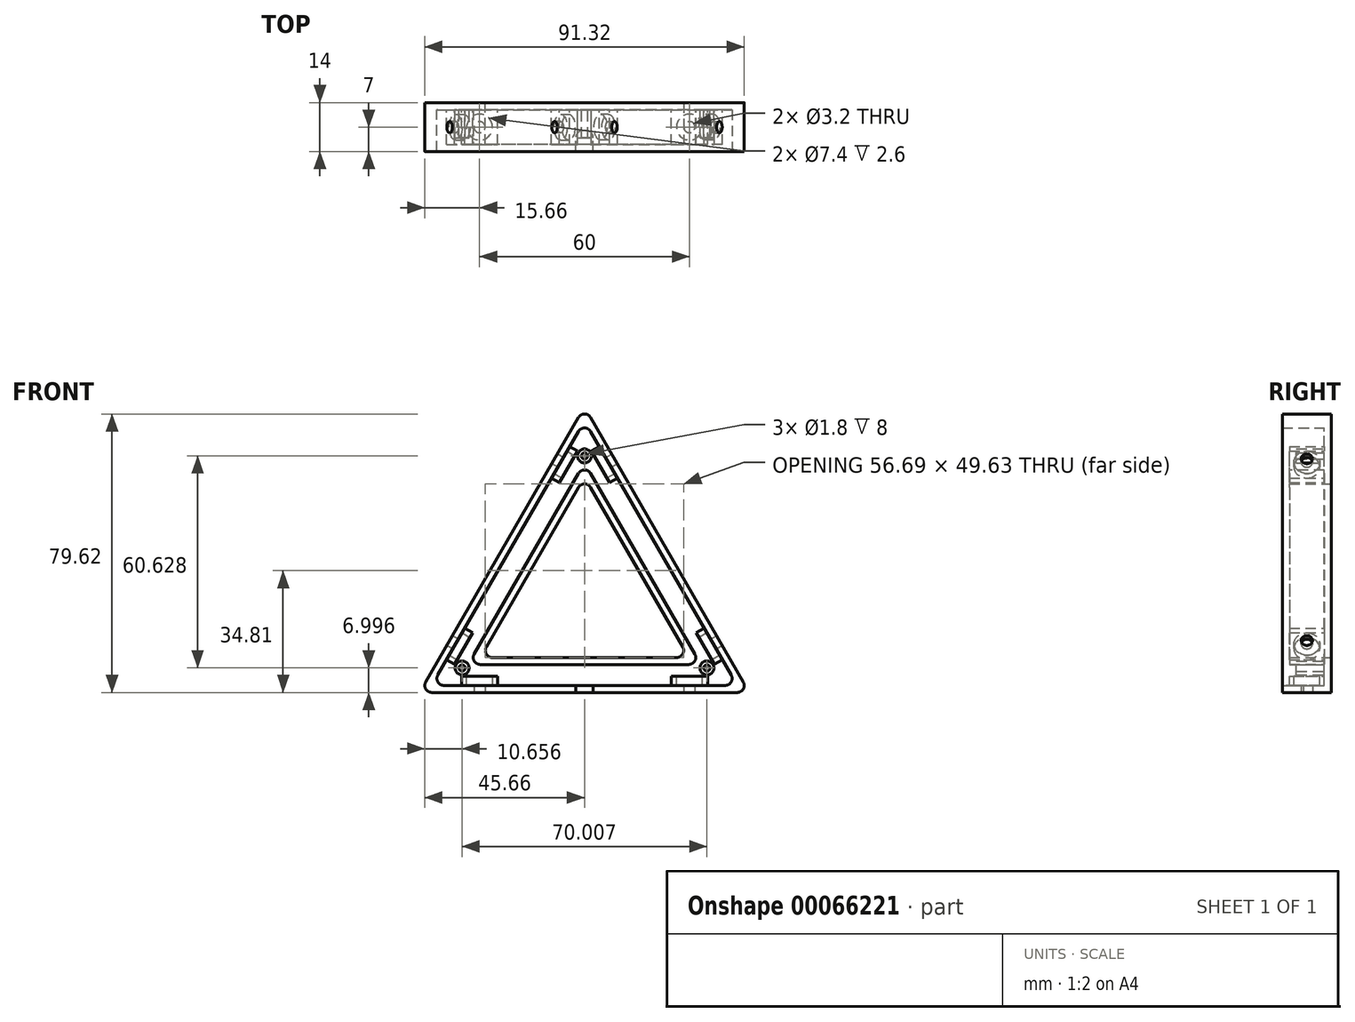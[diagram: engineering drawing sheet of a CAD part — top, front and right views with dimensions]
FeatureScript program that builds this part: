
annotation { "Feature Type Name" : "Feature", "Feature Type Description" : "" }
export const myFeature = defineFeature(function(context is Context, id is Id, definition is map)
    precondition{}
    {
        {
            var Q0;
            Q0=qCreatedBy(makeId("Front.planeOp"),FACE);
            var sketch = newSketch(context, id + "F0", { "sketchPlane" : qUnion([Q0])});
            skLineSegment(sketch, "E0", {"start": v(0, 40.81) * mm, "end": v(-47.13, -40.81) * mm, "construction": true});
            skLineSegment(sketch, "E1", {"start": v(0, 40.81) * mm, "end": v(47.13, -40.81) * mm, "construction": true});
            skLineSegment(sketch, "E2", {"start": v(47.13, -40.81) * mm, "end": v(-47.13, -40.81) * mm, "construction": true});
            skLineSegment(sketch, "E3", {"start": v(0, 40.81) * mm, "end": v(-47.13, -40.81) * mm});
            skLineSegment(sketch, "E4", {"start": v(47.13, -40.81) * mm, "end": v(-47.13, -40.81) * mm});
            skLineSegment(sketch, "E5", {"start": v(0, 40.81) * mm, "end": v(47.13, -40.81) * mm});
            skLineSegment(sketch, "E6", {"start": v(0, 40.81) * mm, "end": v(0, -40.81) * mm, "construction": true});
            skLineSegment(sketch, "E7", {"start": v(0, -40.81) * mm, "end": v(0, 0) * mm, "construction": true});
            skLineSegment(sketch, "E8.0", {"start": v(0, 20.81) * mm, "end": v(29.8, -30.81) * mm});
            skLineSegment(sketch, "E8.1", {"start": v(0, 20.81) * mm, "end": v(-29.8, -30.81) * mm});
            skLineSegment(sketch, "E8.2", {"start": v(29.8, -30.81) * mm, "end": v(-29.8, -30.81) * mm});
            skSolve(sketch);
        }
        {
            var Q0;
            Q0=qSketchRegion(id+"F0",true);
            extrude(context, id + "F1", {"entities" : qUnion([Q0]), "depth" : 2 * mm});
        }
        {
            var Q0;
            Q0=makeQuery(id+"F1.opExtrude","CAP_FACE",FACE,{"disambiguationData":[OSD([sQuery(id+"F0.wireOp",EDGE,"E3"),sQuery(id+"F0.wireOp",EDGE,"E4"),sQuery(id+"F0.wireOp",EDGE,"E5"),sQuery(id+"F0.wireOp",EDGE,"1c6YzCQz-RSOc-zTex-pMTN-9Ec4khBtqjMo"),sQuery(id+"F0.wireOp",EDGE,"E1i0Fd6E-5Ke1-2Vyi-b1Zw-UHEibEwRgWVJ"),sQuery(id+"F0.wireOp",EDGE,"lRk4sWtj-3Wfv-Gcz0-gw5n-paqTTmhbEHYp")])],"isStart":false});
            var sketch = newSketch(context, id + "F2", { "sketchPlane" : qUnion([Q0])});
            skLineSegment(sketch, "E9", {"start": v(-47.13, -40.81) * mm, "end": v(0, 40.81) * mm});
            skLineSegment(sketch, "E10.0", {"start": v(-43.66, -38.81) * mm, "end": v(0, 36.81) * mm});
            skLineSegment(sketch, "E11", {"start": v(-47.13, -40.81) * mm, "end": v(47.13, -40.81) * mm});
            skLineSegment(sketch, "E12.0", {"start": v(-43.66, -38.81) * mm, "end": v(43.66, -38.81) * mm});
            skLineSegment(sketch, "E13.MirrorCS", {"start": v(47.13, -40.81) * mm, "end": v(0, 40.81) * mm});
            skLineSegment(sketch, "E14.MirrorCS", {"start": v(43.66, -38.81) * mm, "end": v(0, 36.81) * mm});
            skSolve(sketch);
        }
        {
            var Q0;
            Q0=qSketchRegion(id+"F2",true);
            extrude(context, id + "F3", {"entities" : qUnion([Q0]), "operationType" : NewBodyOperationType.ADD, "depth" : 12 * mm});
        }
        {
            var Q0;
            Q0=makeQuery(id+"F1.opExtrude","CAP_FACE",FACE,{"disambiguationData":[OSD([sQuery(id+"F0.wireOp",EDGE,"E3"),sQuery(id+"F0.wireOp",EDGE,"E4"),sQuery(id+"F0.wireOp",EDGE,"E5"),sQuery(id+"F0.wireOp",EDGE,"1c6YzCQz-RSOc-zTex-pMTN-9Ec4khBtqjMo"),sQuery(id+"F0.wireOp",EDGE,"E1i0Fd6E-5Ke1-2Vyi-b1Zw-UHEibEwRgWVJ"),sQuery(id+"F0.wireOp",EDGE,"lRk4sWtj-3Wfv-Gcz0-gw5n-paqTTmhbEHYp")])],"isStart":false});
            var sketch = newSketch(context, id + "F4", { "sketchPlane" : qUnion([Q0])});
            skLineSegment(sketch, "E15.0", {"start": v(0, 20.81) * mm, "end": v(29.8, -30.81) * mm});
            skLineSegment(sketch, "E15.1", {"start": v(0, 20.81) * mm, "end": v(-29.8, -30.81) * mm});
            skLineSegment(sketch, "E15.2", {"start": v(29.8, -30.81) * mm, "end": v(-29.8, -30.81) * mm});
            skLineSegment(sketch, "E16.0", {"start": v(0, 24.81) * mm, "end": v(33.27, -32.81) * mm});
            skLineSegment(sketch, "E16.1", {"start": v(0, 24.81) * mm, "end": v(-33.27, -32.81) * mm});
            skLineSegment(sketch, "E16.2", {"start": v(33.27, -32.81) * mm, "end": v(-33.27, -32.81) * mm});
            skSolve(sketch);
        }
        {
            var Q0;
            Q0=qSketchRegion(id+"F4",true);
            extrude(context, id + "F5", {"entities" : qUnion([Q0]), "operationType" : NewBodyOperationType.ADD, "depth" : 10 * mm});
        }
        {
            var Q0;
            Q0=makeQuery(id+"F3.boolean.opBoolean","MERGE",EDGE,{"derivedFrom":[makeQuery(id+"F1.opExtrude","SWEPT_EDGE",EDGE,{"disambiguationData":[OSD([sQuery(id+"F0.wireOp",EDGE,"E4"),sQuery(id+"F0.wireOp",EDGE,"E5")])]}),makeQuery(id+"F3.opExtrude","SWEPT_EDGE",EDGE,{"disambiguationData":[OSD([sQuery(id+"F2.wireOp",EDGE,"E11"),sQuery(id+"F2.wireOp",EDGE,"E13.MirrorCS")])]})]});
            var Q1;
            Q1=makeQuery(id+"F3.boolean.opBoolean","MERGE",EDGE,{"derivedFrom":[makeQuery(id+"F1.opExtrude","SWEPT_EDGE",EDGE,{"disambiguationData":[OSD([sQuery(id+"F0.wireOp",EDGE,"E3"),sQuery(id+"F0.wireOp",EDGE,"E4")])]}),makeQuery(id+"F3.opExtrude","SWEPT_EDGE",EDGE,{"disambiguationData":[OSD([sQuery(id+"F2.wireOp",EDGE,"E9"),sQuery(id+"F2.wireOp",EDGE,"E11")])]})]});
            var Q2;
            Q2=makeQuery(id+"F3.boolean.opBoolean","MERGE",EDGE,{"derivedFrom":[makeQuery(id+"F1.opExtrude","SWEPT_EDGE",EDGE,{"disambiguationData":[OSD([sQuery(id+"F0.wireOp",EDGE,"E3"),sQuery(id+"F0.wireOp",EDGE,"E5")])]}),makeQuery(id+"F3.opExtrude","SWEPT_EDGE",EDGE,{"disambiguationData":[OSD([sQuery(id+"F2.wireOp",EDGE,"E9"),sQuery(id+"F2.wireOp",EDGE,"E13.MirrorCS")])]})]});
            var Q3;
            Q3=makeQuery(id+"F5.opExtrude","SWEPT_EDGE",EDGE,{"disambiguationData":[OSD([sQuery(id+"F4.wireOp",EDGE,"777d23ab-cff7-4353-932e-786e568167e6.0"),sQuery(id+"F4.wireOp",EDGE,"777d23ab-cff7-4353-932e-786e568167e6.1")])]});
            var Q4;
            Q4=makeQuery(id+"F5.opExtrude","SWEPT_EDGE",EDGE,{"disambiguationData":[OSD([sQuery(id+"F4.wireOp",EDGE,"777d23ab-cff7-4353-932e-786e568167e6.1"),sQuery(id+"F4.wireOp",EDGE,"777d23ab-cff7-4353-932e-786e568167e6.2")])]});
            var Q5;
            Q5=makeQuery(id+"F5.opExtrude","SWEPT_EDGE",EDGE,{"disambiguationData":[OSD([sQuery(id+"F4.wireOp",EDGE,"777d23ab-cff7-4353-932e-786e568167e6.0"),sQuery(id+"F4.wireOp",EDGE,"777d23ab-cff7-4353-932e-786e568167e6.2")])]});
            var Q6;
            Q6=makeQuery(id+"F5.boolean.opBoolean","MERGE",EDGE,{"derivedFrom":[makeQuery(id+"F1.opExtrude","SWEPT_EDGE",EDGE,{"disambiguationData":[OSD([sQuery(id+"F0.wireOp",EDGE,"E8.1"),sQuery(id+"F0.wireOp",EDGE,"E8.2")])]}),makeQuery(id+"F5.opExtrude","SWEPT_EDGE",EDGE,{"disambiguationData":[OSD([sQuery(id+"F4.wireOp",EDGE,"E15.1"),sQuery(id+"F4.wireOp",EDGE,"E15.2")])]})]});
            var Q7;
            Q7=makeQuery(id+"F3.opExtrude","SWEPT_EDGE",EDGE,{"disambiguationData":[OSD([sQuery(id+"F2.wireOp",EDGE,"E10.0"),sQuery(id+"F2.wireOp",EDGE,"E12.0")])]});
            var Q8;
            Q8=makeQuery(id+"F5.opExtrude","SWEPT_EDGE",EDGE,{"disambiguationData":[OSD([sQuery(id+"F4.wireOp",EDGE,"E16.0"),sQuery(id+"F4.wireOp",EDGE,"E16.1")])]});
            var Q9;
            Q9=makeQuery(id+"F5.boolean.opBoolean","MERGE",EDGE,{"derivedFrom":[makeQuery(id+"F1.opExtrude","SWEPT_EDGE",EDGE,{"disambiguationData":[OSD([sQuery(id+"F0.wireOp",EDGE,"E8.0"),sQuery(id+"F0.wireOp",EDGE,"E8.1")])]}),makeQuery(id+"F5.opExtrude","SWEPT_EDGE",EDGE,{"disambiguationData":[OSD([sQuery(id+"F4.wireOp",EDGE,"E15.0"),sQuery(id+"F4.wireOp",EDGE,"E15.1")])]})]});
            var Q10;
            Q10=makeQuery(id+"F3.opExtrude","SWEPT_EDGE",EDGE,{"disambiguationData":[OSD([sQuery(id+"F2.wireOp",EDGE,"E10.0"),sQuery(id+"F2.wireOp",EDGE,"E14.MirrorCS")])]});
            var Q11;
            Q11=makeQuery(id+"F5.opExtrude","SWEPT_EDGE",EDGE,{"disambiguationData":[OSD([sQuery(id+"F4.wireOp",EDGE,"E16.0"),sQuery(id+"F4.wireOp",EDGE,"E16.2")])]});
            var Q12;
            Q12=makeQuery(id+"F5.opExtrude","SWEPT_EDGE",EDGE,{"disambiguationData":[OSD([sQuery(id+"F4.wireOp",EDGE,"E16.1"),sQuery(id+"F4.wireOp",EDGE,"E16.2")])]});
            var Q13;
            Q13=makeQuery(id+"F5.boolean.opBoolean","MERGE",EDGE,{"derivedFrom":[makeQuery(id+"F1.opExtrude","SWEPT_EDGE",EDGE,{"disambiguationData":[OSD([sQuery(id+"F0.wireOp",EDGE,"E8.0"),sQuery(id+"F0.wireOp",EDGE,"E8.2")])]}),makeQuery(id+"F5.opExtrude","SWEPT_EDGE",EDGE,{"disambiguationData":[OSD([sQuery(id+"F4.wireOp",EDGE,"E15.0"),sQuery(id+"F4.wireOp",EDGE,"E15.2")])]})]});
            var Q14;
            Q14=makeQuery(id+"F3.opExtrude","SWEPT_EDGE",EDGE,{"disambiguationData":[OSD([sQuery(id+"F2.wireOp",EDGE,"E12.0"),sQuery(id+"F2.wireOp",EDGE,"E14.MirrorCS")])]});
            fillet(context, id + "F6", {"entities" : qUnion([Q0, Q1, Q2, Q3, Q4, Q5, Q6, Q7, Q8, Q9, Q10, Q11, Q12, Q13, Q14]), "radius" : 2 * mm, "tangentPropagation" : true, "allowEdgeOverflow" : false});
        }
        {
            var Q0;
            Q0=makeQuery(id+"F1.opExtrude","CAP_FACE",FACE,{"disambiguationData":[OSD([sQuery(id+"F0.wireOp",EDGE,"E3"),sQuery(id+"F0.wireOp",EDGE,"E4"),sQuery(id+"F0.wireOp",EDGE,"E5"),sQuery(id+"F0.wireOp",EDGE,"E8.0"),sQuery(id+"F0.wireOp",EDGE,"E8.1"),sQuery(id+"F0.wireOp",EDGE,"E8.2")])],"isStart":false});
            var sketch = newSketch(context, id + "F7", { "sketchPlane" : qUnion([Q0])});
            skLineSegment(sketch, "E17", {"start": v(-1.73, 33.81) * mm, "end": v(-4.23, 29.48) * mm, "construction": true});
            skLineSegment(sketch, "E18", {"start": v(-4.23, 29.48) * mm, "end": v(-9.43, 20.48) * mm, "construction": true});
            skLineSegment(sketch, "E19", {"start": v(-9.43, 20.48) * mm, "end": v(-34.23, -22.48) * mm, "construction": true});
            skLineSegment(sketch, "E20", {"start": v(-34.23, -22.48) * mm, "end": v(-39.43, -31.48) * mm, "construction": true});
            skLineSegment(sketch, "E21", {"start": v(-39.43, -31.48) * mm, "end": v(-41.93, -35.81) * mm, "construction": true});
            skLineSegment(sketch, "E22", {"start": v(-41.93, -37.81) * mm, "end": v(21.83, -1) * mm, "construction": true});
            skLineSegment(sketch, "E23", {"start": v(-4.23, 29.48) * mm, "end": v(-1.98, 28.18) * mm, "construction": true});
            skLineSegment(sketch, "E24", {"start": v(-34.23, -22.48) * mm, "end": v(-31.98, -23.78) * mm});
            skLineSegment(sketch, "E25", {"start": v(-9.43, 20.48) * mm, "end": v(-7.18, 19.18) * mm, "construction": true});
            skLineSegment(sketch, "E26", {"start": v(-39.43, -31.48) * mm, "end": v(-37.18, -32.78) * mm});
            skLineSegment(sketch, "E27", {"start": v(-7.18, 19.18) * mm, "end": v(-1.98, 28.18) * mm});
            skLineSegment(sketch, "E28", {"start": v(-4.23, 29.48) * mm, "end": v(-1.98, 28.18) * mm});
            skLineSegment(sketch, "E29", {"start": v(-7.18, 19.18) * mm, "end": v(-9.43, 20.48) * mm});
            skLineSegment(sketch, "E30", {"start": v(-9.43, 20.48) * mm, "end": v(-4.23, 29.48) * mm});
            skLineSegment(sketch, "E31", {"start": v(-31.98, -23.78) * mm, "end": v(-37.18, -32.78) * mm});
            skLineSegment(sketch, "E32", {"start": v(-39.43, -31.48) * mm, "end": v(-34.23, -22.48) * mm});
            skLineSegment(sketch, "E33.MirrorCS", {"start": v(4.23, 29.48) * mm, "end": v(1.98, 28.18) * mm, "construction": true});
            skLineSegment(sketch, "E34.MirrorCS", {"start": v(9.43, 20.48) * mm, "end": v(7.18, 19.18) * mm, "construction": true});
            skLineSegment(sketch, "E35.MirrorCS", {"start": v(4.23, 29.48) * mm, "end": v(1.98, 28.18) * mm});
            skLineSegment(sketch, "E36.MirrorCS", {"start": v(7.18, 19.18) * mm, "end": v(9.43, 20.48) * mm});
            skLineSegment(sketch, "E37.MirrorCS", {"start": v(34.23, -22.48) * mm, "end": v(31.98, -23.78) * mm});
            skLineSegment(sketch, "E38.MirrorCS", {"start": v(39.43, -31.48) * mm, "end": v(37.18, -32.78) * mm});
            skLineSegment(sketch, "E39.MirrorCS", {"start": v(4.23, 29.48) * mm, "end": v(9.43, 20.48) * mm, "construction": true});
            skLineSegment(sketch, "E40.MirrorCS", {"start": v(34.23, -22.48) * mm, "end": v(39.43, -31.48) * mm, "construction": true});
            skLineSegment(sketch, "E41.MirrorCS", {"start": v(9.43, 20.48) * mm, "end": v(34.23, -22.48) * mm, "construction": true});
            skLineSegment(sketch, "E42.MirrorCS", {"start": v(39.43, -31.48) * mm, "end": v(41.93, -35.81) * mm, "construction": true});
            skLineSegment(sketch, "E43.MirrorCS", {"start": v(1.73, 33.81) * mm, "end": v(4.23, 29.48) * mm, "construction": true});
            skLineSegment(sketch, "E44.MirrorCS", {"start": v(39.43, -31.48) * mm, "end": v(34.23, -22.48) * mm});
            skLineSegment(sketch, "E45.MirrorCS", {"start": v(31.98, -23.78) * mm, "end": v(37.18, -32.78) * mm});
            skLineSegment(sketch, "E46.MirrorCS", {"start": v(9.43, 20.48) * mm, "end": v(4.23, 29.48) * mm});
            skLineSegment(sketch, "E47.MirrorCS", {"start": v(7.18, 19.18) * mm, "end": v(1.98, 28.18) * mm});
            skLineSegment(sketch, "E48.MirrorCS", {"start": v(35.2, -38.81) * mm, "end": v(35.2, -36.21) * mm, "construction": true});
            skLineSegment(sketch, "E49.MirrorCS", {"start": v(24.8, -38.81) * mm, "end": v(24.8, -36.21) * mm, "construction": true});
            skLineSegment(sketch, "E50.MirrorCS", {"start": v(35.2, -38.81) * mm, "end": v(35.2, -36.21) * mm});
            skLineSegment(sketch, "E51.MirrorCS", {"start": v(24.8, -36.21) * mm, "end": v(24.8, -38.81) * mm});
            skLineSegment(sketch, "E52.MirrorCS", {"start": v(-24.8, -38.81) * mm, "end": v(-24.8, -36.21) * mm});
            skLineSegment(sketch, "E53.MirrorCS", {"start": v(-35.2, -38.81) * mm, "end": v(-35.2, -36.21) * mm});
            skLineSegment(sketch, "E54.MirrorCS", {"start": v(35.2, -38.81) * mm, "end": v(24.8, -38.81) * mm, "construction": true});
            skLineSegment(sketch, "E55.MirrorCS", {"start": v(-24.8, -38.81) * mm, "end": v(-35.2, -38.81) * mm, "construction": true});
            skLineSegment(sketch, "E56.MirrorCS", {"start": v(40.2, -38.81) * mm, "end": v(35.2, -38.81) * mm, "construction": true});
            skLineSegment(sketch, "E57.MirrorCS", {"start": v(-35.2, -38.81) * mm, "end": v(-24.8, -38.81) * mm});
            skLineSegment(sketch, "E58.MirrorCS", {"start": v(-24.8, -36.21) * mm, "end": v(-35.2, -36.21) * mm});
            skLineSegment(sketch, "E59.MirrorCS", {"start": v(24.8, -38.81) * mm, "end": v(35.2, -38.81) * mm});
            skLineSegment(sketch, "E60.MirrorCS", {"start": v(-35.2, -38.81) * mm, "end": v(-40.2, -38.81) * mm, "construction": true});
            skLineSegment(sketch, "E61.MirrorCS", {"start": v(24.8, -38.81) * mm, "end": v(-24.8, -38.81) * mm, "construction": true});
            skLineSegment(sketch, "E62.MirrorCS", {"start": v(24.8, -36.21) * mm, "end": v(35.2, -36.21) * mm});
            skPoint(sketch, "E63", {"position": v(-36.83, -26.98) * mm});
            skPoint(sketch, "E64", {"position": v(-6.83, 24.98) * mm});
            skSolve(sketch);
        }
        {
            var Q0;
            Q0=qSketchRegion(id+"F7",true);
            extrude(context, id + "F8", {"entities" : qUnion([Q0]), "operationType" : NewBodyOperationType.ADD, "depth" : 10 * mm});
        }
        {
            var Q0;
            Q0=makeQuery(id+"F3.boolean.opBoolean","MERGE",FACE,{"derivedFrom":[makeQuery(id+"F1.opExtrude","SWEPT_FACE",FACE,{"disambiguationData":[OSD([sQuery(id+"F0.wireOp",EDGE,"E4")])]}),makeQuery(id+"F3.opExtrude","SWEPT_FACE",FACE,{"disambiguationData":[OSD([sQuery(id+"F2.wireOp",EDGE,"E11")])]})]});
            var sketch = newSketch(context, id + "F9", { "sketchPlane" : qUnion([Q0])});
            skLineSegment(sketch, "E65", {"start": v(-43.66, 14) * mm, "end": v(43.66, 14) * mm, "construction": true});
            skLineSegment(sketch, "E66", {"start": v(43.66, 14) * mm, "end": v(0, 14) * mm, "construction": true});
            skLineSegment(sketch, "E67", {"start": v(0, 14) * mm, "end": v(2.5, 14) * mm, "construction": true});
            skLineSegment(sketch, "E68", {"start": v(0, 14) * mm, "end": v(-2.5, 14) * mm, "construction": true});
            skLineSegment(sketch, "E69", {"start": v(-2.5, 14) * mm, "end": v(-2.5, 8) * mm, "construction": true});
            skLineSegment(sketch, "E70.bottom", {"start": v(2.5, 14) * mm, "end": v(-2.5, 14) * mm});
            skLineSegment(sketch, "E70.top", {"start": v(2.5, 8) * mm, "end": v(-2.5, 8) * mm});
            skLineSegment(sketch, "E70.left", {"start": v(2.5, 14) * mm, "end": v(2.5, 8) * mm});
            skLineSegment(sketch, "E70.right", {"start": v(-2.5, 14) * mm, "end": v(-2.5, 8) * mm});
            skLineSegment(sketch, "E71.0", {"start": v(-24.8, 12) * mm, "end": v(-24.8, 2) * mm, "construction": true});
            skLineSegment(sketch, "E71.1", {"start": v(-35.2, 12) * mm, "end": v(-35.2, 2) * mm, "construction": true});
            skLineSegment(sketch, "E71.2", {"start": v(24.8, 12) * mm, "end": v(24.8, 2) * mm, "construction": true});
            skLineSegment(sketch, "E71.3", {"start": v(35.2, 12) * mm, "end": v(35.2, 2) * mm, "construction": true});
            skLineSegment(sketch, "E72", {"start": v(-35.2, 7) * mm, "end": v(-24.8, 7) * mm, "construction": true});
            skLineSegment(sketch, "E73", {"start": v(-24.8, 7) * mm, "end": v(-30, 7) * mm, "construction": true});
            skLineSegment(sketch, "E74", {"start": v(-30, 7) * mm, "end": v(24.8, 7) * mm, "construction": true});
            skLineSegment(sketch, "E75", {"start": v(24.8, 7) * mm, "end": v(35.2, 7) * mm, "construction": true});
            skLineSegment(sketch, "E76", {"start": v(35.2, 7) * mm, "end": v(30, 7) * mm, "construction": true});
            skCircle(sketch, "E77", {"center": v(-30, 7) * mm, "radius": 1.6 * mm});
            skCircle(sketch, "E78", {"center": v(30, 7) * mm, "radius": 1.6 * mm});
            skSolve(sketch);
        }
        {
            var Q0;
            Q0=qSketchRegion(id+"F9",true);
            extrude(context, id + "F10", {"entities" : qUnion([Q0]), "operationType" : NewBodyOperationType.REMOVE, "oppositeDirection" : true, "depth" : 5 * mm});
        }
        {
            var Q0;
            Q0=makeQuery(id+"F3.boolean.opBoolean","MERGE",FACE,{"derivedFrom":[makeQuery(id+"F1.opExtrude","SWEPT_FACE",FACE,{"disambiguationData":[OSD([sQuery(id+"F0.wireOp",EDGE,"E5")])]}),makeQuery(id+"F3.opExtrude","SWEPT_FACE",FACE,{"disambiguationData":[OSD([sQuery(id+"F2.wireOp",EDGE,"E13.MirrorCS")])]})]});
            var sketch = newSketch(context, id + "F11", { "sketchPlane" : qUnion([Q0])});
            skLineSegment(sketch, "E79", {"start": v(-14, 31.88) * mm, "end": v(-14, -55.45) * mm, "construction": true});
            skLineSegment(sketch, "E80", {"start": v(-14, -55.45) * mm, "end": v(-14, -11.78) * mm, "construction": true});
            skLineSegment(sketch, "E81", {"start": v(-14, -11.78) * mm, "end": v(-14, -9.28) * mm, "construction": true});
            skLineSegment(sketch, "E82", {"start": v(-14, -9.28) * mm, "end": v(-14, -14.28) * mm, "construction": true});
            skLineSegment(sketch, "E83", {"start": v(-14, -14.28) * mm, "end": v(-8, -14.28) * mm, "construction": true});
            skLineSegment(sketch, "E84.bottom", {"start": v(-14, -9.28) * mm, "end": v(-8, -9.28) * mm, "construction": true});
            skLineSegment(sketch, "E84.right", {"start": v(-8, -9.28) * mm, "end": v(-8, -14.28) * mm, "construction": true});
            skLineSegment(sketch, "E85.0", {"start": v(-12, 13.02) * mm, "end": v(-2, 13.02) * mm, "construction": true});
            skLineSegment(sketch, "E85.1", {"start": v(-12, 23.42) * mm, "end": v(-2, 23.42) * mm, "construction": true});
            skLineSegment(sketch, "E85.2", {"start": v(-12, -46.98) * mm, "end": v(-2, -46.98) * mm, "construction": true});
            skLineSegment(sketch, "E85.3", {"start": v(-12, -36.58) * mm, "end": v(-2, -36.58) * mm, "construction": true});
            skLineSegment(sketch, "E86", {"start": v(-7, -46.98) * mm, "end": v(-7, -36.58) * mm, "construction": true});
            skLineSegment(sketch, "E87", {"start": v(-7, -36.58) * mm, "end": v(-7, -41.78) * mm, "construction": true});
            skLineSegment(sketch, "E88", {"start": v(-7, -41.78) * mm, "end": v(-7, 13.02) * mm, "construction": true});
            skLineSegment(sketch, "E89", {"start": v(-7, 13.02) * mm, "end": v(-7, 23.42) * mm, "construction": true});
            skLineSegment(sketch, "E90", {"start": v(-7, 23.42) * mm, "end": v(-7, 18.22) * mm, "construction": true});
            skCircle(sketch, "E91", {"center": v(-7, 18.22) * mm, "radius": 1.6 * mm});
            skCircle(sketch, "E92", {"center": v(-7, -41.78) * mm, "radius": 1.6 * mm});
            skSolve(sketch);
        }
        {
            var Q0;
            Q0=qSketchRegion(id+"F11",true);
            extrude(context, id + "F12", {"entities" : qUnion([Q0]), "operationType" : NewBodyOperationType.REMOVE, "oppositeDirection" : true, "depth" : 5 * mm});
        }
        {
            var Q0;
            Q0=makeQuery(id+"F3.boolean.opBoolean","MERGE",FACE,{"derivedFrom":[makeQuery(id+"F1.opExtrude","SWEPT_FACE",FACE,{"disambiguationData":[OSD([sQuery(id+"F0.wireOp",EDGE,"E3")])]}),makeQuery(id+"F3.opExtrude","SWEPT_FACE",FACE,{"disambiguationData":[OSD([sQuery(id+"F2.wireOp",EDGE,"E9")])]})]});
            var sketch = newSketch(context, id + "F13", { "sketchPlane" : qUnion([Q0])});
            skLineSegment(sketch, "E93", {"start": v(14, -55.45) * mm, "end": v(14, 31.88) * mm, "construction": true});
            skLineSegment(sketch, "E94", {"start": v(14, 31.88) * mm, "end": v(14, -11.78) * mm, "construction": true});
            skLineSegment(sketch, "E95", {"start": v(14, -11.78) * mm, "end": v(14, -9.28) * mm, "construction": true});
            skLineSegment(sketch, "E96", {"start": v(14, -9.28) * mm, "end": v(14, -14.28) * mm, "construction": true});
            skLineSegment(sketch, "E97", {"start": v(14, -14.28) * mm, "end": v(8, -14.28) * mm, "construction": true});
            skLineSegment(sketch, "E98.bottom", {"start": v(14, -9.28) * mm, "end": v(8, -9.28) * mm, "construction": true});
            skLineSegment(sketch, "E98.right", {"start": v(8, -9.28) * mm, "end": v(8, -14.28) * mm, "construction": true});
            skLineSegment(sketch, "E99.0", {"start": v(12, 13.02) * mm, "end": v(2, 13.02) * mm, "construction": true});
            skLineSegment(sketch, "E99.1", {"start": v(12, 23.42) * mm, "end": v(2, 23.42) * mm, "construction": true});
            skLineSegment(sketch, "E99.2", {"start": v(12, -36.58) * mm, "end": v(2, -36.58) * mm, "construction": true});
            skLineSegment(sketch, "E99.3", {"start": v(12, -46.98) * mm, "end": v(2, -46.98) * mm, "construction": true});
            skLineSegment(sketch, "E100", {"start": v(7, 23.42) * mm, "end": v(7, 13.02) * mm, "construction": true});
            skLineSegment(sketch, "E101", {"start": v(7, 13.02) * mm, "end": v(7, 18.22) * mm, "construction": true});
            skLineSegment(sketch, "E102", {"start": v(7, 18.22) * mm, "end": v(7, -36.58) * mm, "construction": true});
            skLineSegment(sketch, "E103", {"start": v(7, -36.58) * mm, "end": v(7, -46.98) * mm, "construction": true});
            skLineSegment(sketch, "E104", {"start": v(7, -46.98) * mm, "end": v(7, -41.78) * mm, "construction": true});
            skCircle(sketch, "E105", {"center": v(7, 18.22) * mm, "radius": 1.6 * mm});
            skCircle(sketch, "E106", {"center": v(7, -41.78) * mm, "radius": 1.6 * mm});
            skSolve(sketch);
        }
        {
            var Q0;
            Q0=qSketchRegion(id+"F13",true);
            extrude(context, id + "F14", {"entities" : qUnion([Q0]), "operationType" : NewBodyOperationType.REMOVE, "oppositeDirection" : true, "depth" : 5 * mm});
        }
        {
            var Q0;
            Q0=makeQuery(id+"F12.boolean.opBoolean","COPY",EDGE,{"derivedFrom":makeQuery(id+"F12.opExtrude","SWEPT_EDGE",EDGE,{"disambiguationData":[OSD([sQuery(id+"F11.wireOp",EDGE,"E83"),sQuery(id+"F11.wireOp",EDGE,"E84.right")])]})});
            var Q1;
            Q1=makeQuery(id+"F14.boolean.opBoolean","COPY",EDGE,{"derivedFrom":makeQuery(id+"F14.opExtrude","SWEPT_EDGE",EDGE,{"disambiguationData":[OSD([sQuery(id+"F13.wireOp",EDGE,"E97"),sQuery(id+"F13.wireOp",EDGE,"E98.right")])]})});
            var Q2;
            Q2=makeQuery(id+"F10.boolean.opBoolean","COPY",EDGE,{"derivedFrom":makeQuery(id+"F10.opExtrude","SWEPT_EDGE",EDGE,{"disambiguationData":[OSD([sQuery(id+"F9.wireOp",EDGE,"E70.top"),sQuery(id+"F9.wireOp",EDGE,"E70.right")])]})});
            var Q3;
            Q3=makeQuery(id+"F12.boolean.opBoolean","COPY",EDGE,{"derivedFrom":makeQuery(id+"F12.opExtrude","SWEPT_EDGE",EDGE,{"disambiguationData":[OSD([sQuery(id+"F11.wireOp",EDGE,"E84.bottom"),sQuery(id+"F11.wireOp",EDGE,"E84.right")])]})});
            var Q4;
            Q4=makeQuery(id+"F14.boolean.opBoolean","COPY",EDGE,{"derivedFrom":makeQuery(id+"F14.opExtrude","SWEPT_EDGE",EDGE,{"disambiguationData":[OSD([sQuery(id+"F13.wireOp",EDGE,"E98.bottom"),sQuery(id+"F13.wireOp",EDGE,"E98.right")])]})});
            var Q5;
            Q5=makeQuery(id+"F10.boolean.opBoolean","COPY",EDGE,{"derivedFrom":makeQuery(id+"F10.opExtrude","SWEPT_EDGE",EDGE,{"disambiguationData":[OSD([sQuery(id+"F9.wireOp",EDGE,"E70.top"),sQuery(id+"F9.wireOp",EDGE,"E70.left")])]})});
            fillet(context, id + "F15", {"entities" : qUnion([Q0, Q1, Q2, Q3, Q4, Q5]), "radius" : 2 * mm, "tangentPropagation" : true, "allowEdgeOverflow" : false});
        }
        {
            var Q0;
            Q0=makeQuery(id+"F8.opExtrude","SWEPT_FACE",FACE,{"disambiguationData":[OSD([sQuery(id+"F7.wireOp",EDGE,"E58.MirrorCS")])]});
            var sketch = newSketch(context, id + "F16", { "sketchPlane" : qUnion([Q0])});
            skCircle(sketch, "E107", {"center": v(30, -7) * mm, "radius": 3.7 * mm});
            skCircle(sketch, "E108", {"center": v(-30, -7) * mm, "radius": 3.7 * mm});
            skSolve(sketch);
        }
        {
            var Q0;
            Q0=qSketchRegion(id+"F16",true);
            extrude(context, id + "F17", {"entities" : qUnion([Q0]), "operationType" : NewBodyOperationType.REMOVE, "oppositeDirection" : true, "depth" : 2.6 * mm});
        }
        {
            var Q0;
            Q0=makeQuery(id+"F8.opExtrude","SWEPT_FACE",FACE,{"disambiguationData":[OSD([sQuery(id+"F7.wireOp",EDGE,"E47.MirrorCS")])]});
            var sketch = newSketch(context, id + "F18", { "sketchPlane" : qUnion([Q0])});
            skCircle(sketch, "E109", {"center": v(7, -41.78) * mm, "radius": 3.7 * mm});
            skCircle(sketch, "E110", {"center": v(7, 18.22) * mm, "radius": 3.7 * mm});
            skSolve(sketch);
        }
        {
            var Q0;
            Q0=qSketchRegion(id+"F18",true);
            extrude(context, id + "F19", {"entities" : qUnion([Q0]), "operationType" : NewBodyOperationType.REMOVE, "oppositeDirection" : true, "depth" : 2.6 * mm});
        }
        {
            var Q0;
            Q0=makeQuery(id+"F8.opExtrude","SWEPT_FACE",FACE,{"disambiguationData":[OSD([sQuery(id+"F7.wireOp",EDGE,"E27")])]});
            var sketch = newSketch(context, id + "F20", { "sketchPlane" : qUnion([Q0])});
            skCircle(sketch, "E111", {"center": v(-7, -41.78) * mm, "radius": 3.7 * mm});
            skCircle(sketch, "E112", {"center": v(-7, 18.22) * mm, "radius": 3.7 * mm});
            skSolve(sketch);
        }
        {
            var Q0;
            Q0=qSketchRegion(id+"F20",true);
            extrude(context, id + "F21", {"entities" : qUnion([Q0]), "operationType" : NewBodyOperationType.REMOVE, "oppositeDirection" : true, "depth" : 2.6 * mm});
        }
        {
            var Q0;
            Q0=makeQuery(id+"F1.opExtrude","CAP_FACE",FACE,{"disambiguationData":[OSD([sQuery(id+"F0.wireOp",EDGE,"E3"),sQuery(id+"F0.wireOp",EDGE,"E4"),sQuery(id+"F0.wireOp",EDGE,"E5"),sQuery(id+"F0.wireOp",EDGE,"1c6YzCQz-RSOc-zTex-pMTN-9Ec4khBtqjMo"),sQuery(id+"F0.wireOp",EDGE,"E1i0Fd6E-5Ke1-2Vyi-b1Zw-UHEibEwRgWVJ"),sQuery(id+"F0.wireOp",EDGE,"lRk4sWtj-3Wfv-Gcz0-gw5n-paqTTmhbEHYp")])],"isStart":false});
            var sketch = newSketch(context, id + "F22", { "sketchPlane" : qUnion([Q0])});
            skCircle(sketch, "E113", {"center": v(0, 26.81) * mm, "radius": 0.9 * mm});
            skCircle(sketch, "E114", {"center": v(0, 26.81) * mm, "radius": 2 * mm});
            skCircle(sketch, "E115", {"center": v(35, -33.81) * mm, "radius": 0.9 * mm});
            skCircle(sketch, "E116", {"center": v(35, -33.81) * mm, "radius": 2 * mm});
            skArc(sketch, "E117.0", {"start": v(-26.34, -30.81) * mm, "mid": v(-28.08, -29.81) * mm, "end": v(-28.08, -27.81) * mm, "construction": true});
            skLineSegment(sketch, "E118", {"start": v(-28.08, -29.81) * mm, "end": v(-41.93, -37.81) * mm, "construction": true});
            skLineSegment(sketch, "E119", {"start": v(-41.93, -37.81) * mm, "end": v(-35, -33.81) * mm, "construction": true});
            skCircle(sketch, "E120", {"center": v(-35, -33.81) * mm, "radius": 2 * mm});
            skCircle(sketch, "E121", {"center": v(-35, -33.81) * mm, "radius": 0.9 * mm});
            skArc(sketch, "E122.0", {"start": v(-1.73, 17.81) * mm, "mid": v(0, 18.81) * mm, "end": v(1.73, 17.81) * mm, "construction": true});
            skLineSegment(sketch, "E123", {"start": v(0, 34.81) * mm, "end": v(0, 18.81) * mm, "construction": true});
            skLineSegment(sketch, "E124", {"start": v(0, 18.81) * mm, "end": v(0, 26.81) * mm, "construction": true});
            skArc(sketch, "E125.0", {"start": v(28.08, -27.81) * mm, "mid": v(28.08, -29.81) * mm, "end": v(26.34, -30.81) * mm, "construction": true});
            skLineSegment(sketch, "E126", {"start": v(28.08, -29.81) * mm, "end": v(41.93, -37.81) * mm, "construction": true});
            skLineSegment(sketch, "E127", {"start": v(41.93, -37.81) * mm, "end": v(35, -33.81) * mm, "construction": true});
            skSolve(sketch);
        }
        {
            var Q0;
            Q0=qSketchRegion(id+"F22",true);
            extrude(context, id + "F23", {"entities" : qUnion([Q0]), "operationType" : NewBodyOperationType.ADD, "depth" : 8 * mm});
        }
    });
